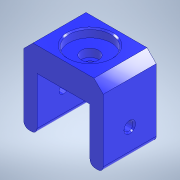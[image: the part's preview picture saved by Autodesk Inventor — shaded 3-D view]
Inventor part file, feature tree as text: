
AUTODESK INVENTOR PART (.ipt)
format: ipt  version: 2022 (Build 260153000, 153)  size: 172,544 bytes
history: native  units: mm
features: sketch x3, extrude x3, hole x2, chamfer x2, projected_geometry x2, fillet x1
ambient origin geometry x8: Origin, YZ Plane, XZ Plane, XY Plane, X Axis, Y Axis, Z Axis, Center Point
bodies: Solid1 (feature_tree)
feature tree (13):
  sketch  "Sketch1"  dims[d0=30.0mm d1=16.0mm]
  extrude  "Extrusion1"  Depth=30.0mm
  extrude  "Extrusion2"  Depth=6.0mm TaperAngle=0.0deg
  hole  "Hole1"  [1 undecoded]
  extrude  "Extrusion3"  Depth=5.0mm
  chamfer  "Chamfer1"  Distance=20.0mm
  fillet  "Fillet1"  Radius=2.0mm
  hole  "Hole2"  [1 undecoded]
  chamfer  "Chamfer2"  Distance=2.0mm Angle=45.0deg
  sketch  "Sketch2"  dims[d2=20.0mm d3=6.0mm d4=0.0mm]
  projected_geometry  "Projected Loop1"
  sketch  "Sketch3"  dims[d5=3.2mm d6=0.0mm d7=3.4mm d8=6.0mm d9=6.5mm d10=3.05mm d11=90.0deg d12=10.0mm d13=0.0mm d14=5.0mm d15=5.0mm d16=20.0mm d17=0.0mm d18=3.5mm d19=2.0mm d20=45.0deg d21=2.0mm d22=3.4mm d23=6.0mm d24=6.5mm d25=3.05mm d26=14.3117mm d27=10.0mm d28=0.0mm d29=0.5mm d30=2.0mm d31=45.0deg]
  projected_geometry  "Projected Loop2"
note: 2 required parameter values undecoded (feature->parameter linkage not recoverable at this tier; creation-order binding heuristic only, values carry confidence <= 0.55)
